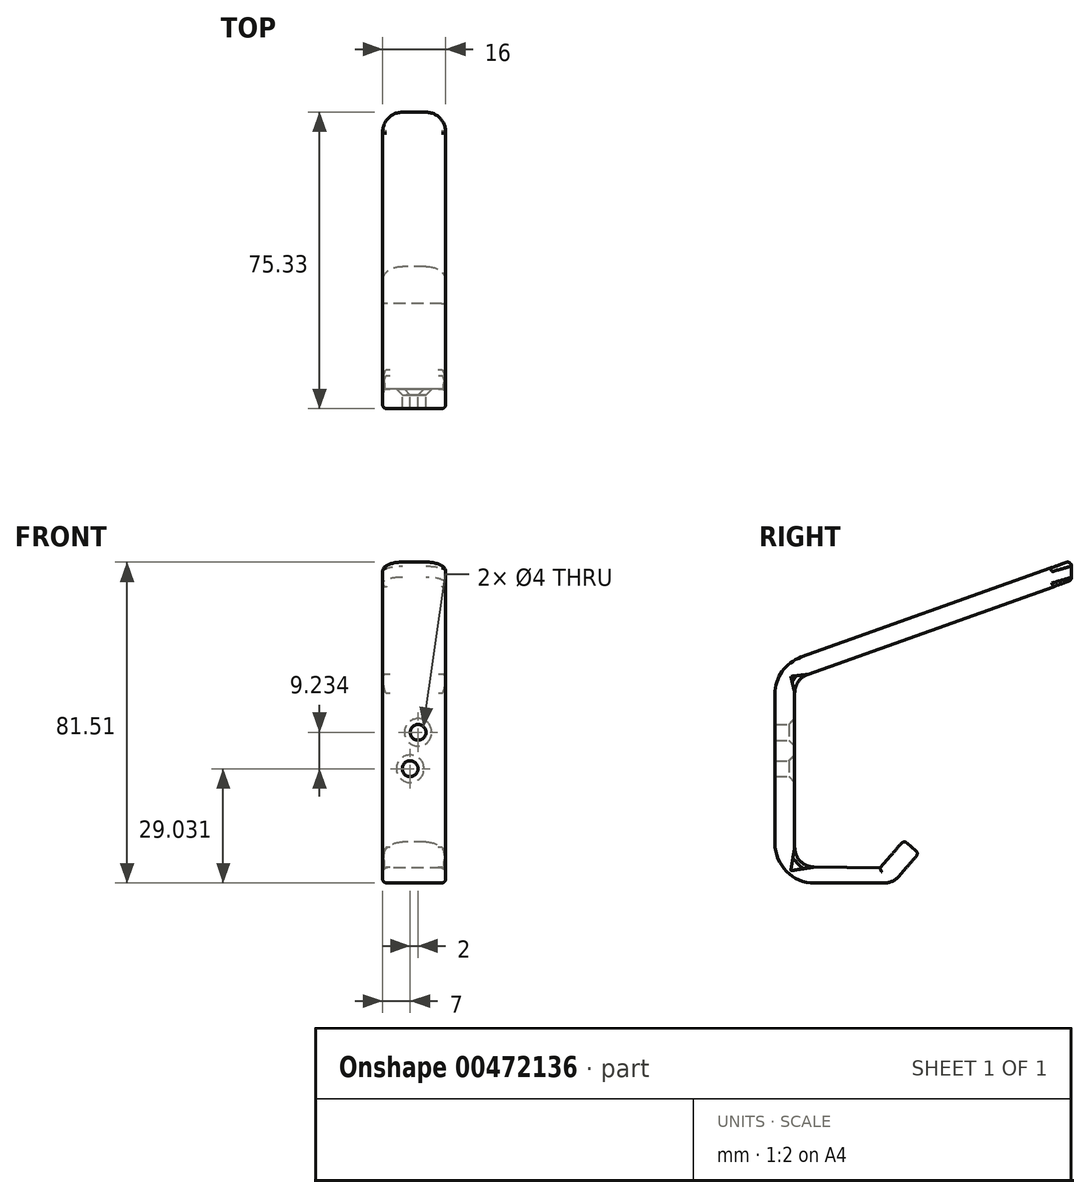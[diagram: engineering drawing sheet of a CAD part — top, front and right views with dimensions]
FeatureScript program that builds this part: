
annotation { "Feature Type Name" : "Feature", "Feature Type Description" : "" }
export const myFeature = defineFeature(function(context is Context, id is Id, definition is map)
    precondition{}
    {
        {
            var Q0;
            Q0=qCreatedBy(makeId("Right.planeOp"),FACE);
            var sketch = newSketch(context, id + "F0", { "sketchPlane" : qUnion([Q0])});
            skLineSegment(sketch, "E0", {"start": v(0, 0) * mm, "end": v(0, 55) * mm});
            skLineSegment(sketch, "E1", {"start": v(0, 0) * mm, "end": v(30, 0) * mm});
            skLineSegment(sketch, "E2", {"start": v(30, 0) * mm, "end": v(36.55, 7.55) * mm});
            skLineSegment(sketch, "E3", {"start": v(0, 55) * mm, "end": v(75.33, 81.93) * mm});
            skLineSegment(sketch, "E4", {"start": v(36.55, 7.55) * mm, "end": v(32.78, 10.83) * mm});
            skLineSegment(sketch, "E5", {"start": v(32.78, 10.83) * mm, "end": v(26.66, 3.78) * mm});
            skPoint(sketch, "E5.endSnap0", {"position": v(33.28, 3.78) * mm});
            skLineSegment(sketch, "E6", {"start": v(75.33, 81.93) * mm, "end": v(75.33, 76.93) * mm});
            skLineSegment(sketch, "E7", {"start": v(75.33, 76.93) * mm, "end": v(5, 51.79) * mm});
            skLineSegment(sketch, "E8", {"start": v(5, 4.33) * mm, "end": v(5, 51.79) * mm});
            skPoint(sketch, "E9.end.orphan", {"position": v(0, -21.36) * mm});
            skPoint(sketch, "E9.start.orphan", {"position": v(5, -21.36) * mm});
            skLineSegment(sketch, "E10", {"start": v(5, 4.33) * mm, "end": v(5, 4.1) * mm});
            skLineSegment(sketch, "E11", {"start": v(26.66, 3.78) * mm, "end": v(5, 4.1) * mm});
            skPoint(sketch, "E12.orphan", {"position": v(-9.92, 4.33) * mm});
            skSolve(sketch);
        }
        {
            var Q0;
            Q0=makeQuery(id+"F0.imprint","IMPRINT",FACE,{"disambiguationData":[TD([[makeQuery(id+"F0.imprint","IMPRINT",EDGE,{"derivedFrom":sQuery(id+"F0.wireOp",EDGE,"E0")}),-1.0]])]});
            extrude(context, id + "F1", {"entities" : qUnion([Q0]), "depth" : 16 * mm, "offsetDistance" : 25 * mm});
        }
        {
            var Q0;
            Q0=makeQuery(id+"F1.opExtrude","SWEPT_EDGE",EDGE,{"disambiguationData":[OSD([sQuery(id+"F0.wireOp",EDGE,"E0"),sQuery(id+"F0.wireOp",EDGE,"E1")])]});
            fillet(context, id + "F2", {"entities" : qUnion([Q0]), "radius" : 10 * mm, "tangentPropagation" : true, "allowEdgeOverflow" : false});
        }
        {
            var Q0;
            Q0=makeQuery(id+"F1.opExtrude","SWEPT_EDGE",EDGE,{"disambiguationData":[OSD([sQuery(id+"F0.wireOp",EDGE,"E0"),sQuery(id+"F0.wireOp",EDGE,"E3")])]});
            fillet(context, id + "F3", {"entities" : qUnion([Q0]), "radius" : 10 * mm, "tangentPropagation" : true, "allowEdgeOverflow" : false});
        }
        {
            var Q0;
            Q0=makeQuery(id+"F1.opExtrude","SWEPT_EDGE",EDGE,{"disambiguationData":[OSD([sQuery(id+"F0.wireOp",EDGE,"E1"),sQuery(id+"F0.wireOp",EDGE,"E2")])]});
            fillet(context, id + "F4", {"entities" : qUnion([Q0]), "radius" : 5 * mm, "tangentPropagation" : true, "allowEdgeOverflow" : false});
        }
        {
            var Q0;
            Q0=makeQuery(id+"F1.opExtrude","CAP_EDGE",EDGE,{"disambiguationData":[OSD([sQuery(id+"F0.wireOp",EDGE,"E11")])],"isStart":true});
            fillet(context, id + "F5", {"entities" : qUnion([Q0]), "radius" : 1 * mm, "tangentPropagation" : true, "allowEdgeOverflow" : false});
        }
        {
            var Q0;
            Q0=makeQuery(id+"F1.opExtrude","CAP_EDGE",EDGE,{"disambiguationData":[OSD([sQuery(id+"F0.wireOp",EDGE,"E5")])],"isStart":true});
            var Q1;
            Q1=makeQuery(id+"F1.opExtrude","CAP_EDGE",EDGE,{"disambiguationData":[OSD([sQuery(id+"F0.wireOp",EDGE,"E5")])],"isStart":false});
            var Q2;
            Q2=makeQuery(id+"F1.opExtrude","SWEPT_EDGE",EDGE,{"disambiguationData":[OSD([sQuery(id+"F0.wireOp",EDGE,"E4"),sQuery(id+"F0.wireOp",EDGE,"E5")])]});
            var Q3;
            Q3=makeQuery(id+"F1.opExtrude","CAP_EDGE",EDGE,{"disambiguationData":[OSD([sQuery(id+"F0.wireOp",EDGE,"E11")])],"isStart":false});
            var Q4;
            Q4=makeQuery(id+"F1.opExtrude","CAP_EDGE",EDGE,{"disambiguationData":[OSD([sQuery(id+"F0.wireOp",EDGE,"E8"),sQuery(id+"F0.wireOp",EDGE,"E10")])],"isStart":true});
            var Q5;
            Q5=makeQuery(id+"F1.opExtrude","CAP_EDGE",EDGE,{"disambiguationData":[OSD([sQuery(id+"F0.wireOp",EDGE,"E8"),sQuery(id+"F0.wireOp",EDGE,"E10")])],"isStart":false});
            var Q6;
            Q6=makeQuery(id+"F1.opExtrude","CAP_EDGE",EDGE,{"disambiguationData":[OSD([sQuery(id+"F0.wireOp",EDGE,"E7")])],"isStart":true});
            var Q7;
            Q7=makeQuery(id+"F1.opExtrude","CAP_EDGE",EDGE,{"disambiguationData":[OSD([sQuery(id+"F0.wireOp",EDGE,"E7")])],"isStart":false});
            var Q8;
            Q8=makeQuery(id+"F1.opExtrude","SWEPT_EDGE",EDGE,{"disambiguationData":[OSD([sQuery(id+"F0.wireOp",EDGE,"E6"),sQuery(id+"F0.wireOp",EDGE,"E7")])]});
            fillet(context, id + "F6", {"entities" : qUnion([Q0, Q1, Q2, Q3, Q4, Q5, Q6, Q7, Q8]), "radius" : 1 * mm, "tangentPropagation" : true, "allowEdgeOverflow" : false});
        }
        {
            var Q0;
            Q0=makeQuery(id+"F1.opExtrude","CAP_EDGE",EDGE,{"disambiguationData":[OSD([sQuery(id+"F0.wireOp",EDGE,"E1")])],"isStart":false});
            var Q1;
            {var subQ0=sQuery(id+"F0.wireOp",EDGE,"E2");var subQ1=sQuery(id+"F0.wireOp",EDGE,"E1");Q1=makeQuery(id+"F4.opFillet","BLEND_EDGE",EDGE,{"blendedFrom":[makeQuery(id+"F1.opExtrude","SWEPT_EDGE",EDGE,{"disambiguationData":[OSD([subQ1,subQ0])]}),makeQuery(id+"F1.opExtrude","CAP_FACE",FACE,{"disambiguationData":[OSD([sQuery(id+"F0.wireOp",EDGE,"E0"),subQ1,subQ0,sQuery(id+"F0.wireOp",EDGE,"E3"),sQuery(id+"F0.wireOp",EDGE,"E4"),sQuery(id+"F0.wireOp",EDGE,"E5"),sQuery(id+"F0.wireOp",EDGE,"E6"),sQuery(id+"F0.wireOp",EDGE,"E7"),sQuery(id+"F0.wireOp",EDGE,"E8"),sQuery(id+"F0.wireOp",EDGE,"E10"),sQuery(id+"F0.wireOp",EDGE,"E11")])],"isStart":false})],"blendedInto":[makeQuery(id+"F1.opExtrude","CAP_FACE",FACE,{"disambiguationData":[OSD([sQuery(id+"F0.wireOp",EDGE,"E0"),subQ1,subQ0,sQuery(id+"F0.wireOp",EDGE,"E3"),sQuery(id+"F0.wireOp",EDGE,"E4"),sQuery(id+"F0.wireOp",EDGE,"E5"),sQuery(id+"F0.wireOp",EDGE,"E6"),sQuery(id+"F0.wireOp",EDGE,"E7"),sQuery(id+"F0.wireOp",EDGE,"E8"),sQuery(id+"F0.wireOp",EDGE,"E10"),sQuery(id+"F0.wireOp",EDGE,"E11")])],"isStart":false})]});}
            var Q2;
            Q2=makeQuery(id+"F1.opExtrude","CAP_EDGE",EDGE,{"disambiguationData":[OSD([sQuery(id+"F0.wireOp",EDGE,"E2")])],"isStart":false});
            var Q3;
            Q3=makeQuery(id+"F1.opExtrude","SWEPT_EDGE",EDGE,{"disambiguationData":[OSD([sQuery(id+"F0.wireOp",EDGE,"E2"),sQuery(id+"F0.wireOp",EDGE,"E4")])]});
            var Q4;
            Q4=makeQuery(id+"F1.opExtrude","CAP_EDGE",EDGE,{"disambiguationData":[OSD([sQuery(id+"F0.wireOp",EDGE,"E2")])],"isStart":true});
            var Q5;
            Q5=makeQuery(id+"F1.opExtrude","CAP_EDGE",EDGE,{"disambiguationData":[OSD([sQuery(id+"F0.wireOp",EDGE,"E1")])],"isStart":true});
            var Q6;
            {var subQ0=sQuery(id+"F0.wireOp",EDGE,"E2");var subQ1=sQuery(id+"F0.wireOp",EDGE,"E1");Q6=makeQuery(id+"F4.opFillet","BLEND_EDGE",EDGE,{"blendedFrom":[makeQuery(id+"F1.opExtrude","SWEPT_EDGE",EDGE,{"disambiguationData":[OSD([subQ1,subQ0])]}),makeQuery(id+"F1.opExtrude","CAP_FACE",FACE,{"disambiguationData":[OSD([sQuery(id+"F0.wireOp",EDGE,"E0"),subQ1,subQ0,sQuery(id+"F0.wireOp",EDGE,"E3"),sQuery(id+"F0.wireOp",EDGE,"E4"),sQuery(id+"F0.wireOp",EDGE,"E5"),sQuery(id+"F0.wireOp",EDGE,"E6"),sQuery(id+"F0.wireOp",EDGE,"E7"),sQuery(id+"F0.wireOp",EDGE,"E8"),sQuery(id+"F0.wireOp",EDGE,"E10"),sQuery(id+"F0.wireOp",EDGE,"E11")])],"isStart":true})],"blendedInto":[makeQuery(id+"F1.opExtrude","CAP_FACE",FACE,{"disambiguationData":[OSD([sQuery(id+"F0.wireOp",EDGE,"E0"),subQ1,subQ0,sQuery(id+"F0.wireOp",EDGE,"E3"),sQuery(id+"F0.wireOp",EDGE,"E4"),sQuery(id+"F0.wireOp",EDGE,"E5"),sQuery(id+"F0.wireOp",EDGE,"E6"),sQuery(id+"F0.wireOp",EDGE,"E7"),sQuery(id+"F0.wireOp",EDGE,"E8"),sQuery(id+"F0.wireOp",EDGE,"E10"),sQuery(id+"F0.wireOp",EDGE,"E11")])],"isStart":true})]});}
            var Q7;
            {var subQ0=sQuery(id+"F0.wireOp",EDGE,"E1");var subQ1=sQuery(id+"F0.wireOp",EDGE,"E0");Q7=makeQuery(id+"F2.opFillet","BLEND_EDGE",EDGE,{"blendedFrom":[makeQuery(id+"F1.opExtrude","SWEPT_EDGE",EDGE,{"disambiguationData":[OSD([subQ1,subQ0])]}),makeQuery(id+"F1.opExtrude","CAP_FACE",FACE,{"disambiguationData":[OSD([subQ1,subQ0,sQuery(id+"F0.wireOp",EDGE,"E2"),sQuery(id+"F0.wireOp",EDGE,"E3"),sQuery(id+"F0.wireOp",EDGE,"E4"),sQuery(id+"F0.wireOp",EDGE,"E5"),sQuery(id+"F0.wireOp",EDGE,"E6"),sQuery(id+"F0.wireOp",EDGE,"E7"),sQuery(id+"F0.wireOp",EDGE,"E8"),sQuery(id+"F0.wireOp",EDGE,"E10"),sQuery(id+"F0.wireOp",EDGE,"E11")])],"isStart":false})],"blendedInto":[makeQuery(id+"F1.opExtrude","CAP_FACE",FACE,{"disambiguationData":[OSD([subQ1,subQ0,sQuery(id+"F0.wireOp",EDGE,"E2"),sQuery(id+"F0.wireOp",EDGE,"E3"),sQuery(id+"F0.wireOp",EDGE,"E4"),sQuery(id+"F0.wireOp",EDGE,"E5"),sQuery(id+"F0.wireOp",EDGE,"E6"),sQuery(id+"F0.wireOp",EDGE,"E7"),sQuery(id+"F0.wireOp",EDGE,"E8"),sQuery(id+"F0.wireOp",EDGE,"E10"),sQuery(id+"F0.wireOp",EDGE,"E11")])],"isStart":false})]});}
            var Q8;
            {var subQ0=sQuery(id+"F0.wireOp",EDGE,"E1");var subQ1=sQuery(id+"F0.wireOp",EDGE,"E0");Q8=makeQuery(id+"F2.opFillet","BLEND_EDGE",EDGE,{"blendedFrom":[makeQuery(id+"F1.opExtrude","SWEPT_EDGE",EDGE,{"disambiguationData":[OSD([subQ1,subQ0])]}),makeQuery(id+"F1.opExtrude","CAP_FACE",FACE,{"disambiguationData":[OSD([subQ1,subQ0,sQuery(id+"F0.wireOp",EDGE,"E2"),sQuery(id+"F0.wireOp",EDGE,"E3"),sQuery(id+"F0.wireOp",EDGE,"E4"),sQuery(id+"F0.wireOp",EDGE,"E5"),sQuery(id+"F0.wireOp",EDGE,"E6"),sQuery(id+"F0.wireOp",EDGE,"E7"),sQuery(id+"F0.wireOp",EDGE,"E8"),sQuery(id+"F0.wireOp",EDGE,"E10"),sQuery(id+"F0.wireOp",EDGE,"E11")])],"isStart":true})],"blendedInto":[makeQuery(id+"F1.opExtrude","CAP_FACE",FACE,{"disambiguationData":[OSD([subQ1,subQ0,sQuery(id+"F0.wireOp",EDGE,"E2"),sQuery(id+"F0.wireOp",EDGE,"E3"),sQuery(id+"F0.wireOp",EDGE,"E4"),sQuery(id+"F0.wireOp",EDGE,"E5"),sQuery(id+"F0.wireOp",EDGE,"E6"),sQuery(id+"F0.wireOp",EDGE,"E7"),sQuery(id+"F0.wireOp",EDGE,"E8"),sQuery(id+"F0.wireOp",EDGE,"E10"),sQuery(id+"F0.wireOp",EDGE,"E11")])],"isStart":true})]});}
            var Q9;
            Q9=makeQuery(id+"F1.opExtrude","CAP_EDGE",EDGE,{"disambiguationData":[OSD([sQuery(id+"F0.wireOp",EDGE,"E0")])],"isStart":true});
            var Q10;
            Q10=makeQuery(id+"F1.opExtrude","CAP_EDGE",EDGE,{"disambiguationData":[OSD([sQuery(id+"F0.wireOp",EDGE,"E0")])],"isStart":false});
            var Q11;
            {var subQ0=sQuery(id+"F0.wireOp",EDGE,"E3");var subQ1=sQuery(id+"F0.wireOp",EDGE,"E0");Q11=makeQuery(id+"F3.opFillet","BLEND_EDGE",EDGE,{"blendedFrom":[makeQuery(id+"F1.opExtrude","SWEPT_EDGE",EDGE,{"disambiguationData":[OSD([subQ1,subQ0])]}),makeQuery(id+"F1.opExtrude","CAP_FACE",FACE,{"disambiguationData":[OSD([subQ1,sQuery(id+"F0.wireOp",EDGE,"E1"),sQuery(id+"F0.wireOp",EDGE,"E2"),subQ0,sQuery(id+"F0.wireOp",EDGE,"E4"),sQuery(id+"F0.wireOp",EDGE,"E5"),sQuery(id+"F0.wireOp",EDGE,"E6"),sQuery(id+"F0.wireOp",EDGE,"E7"),sQuery(id+"F0.wireOp",EDGE,"E8"),sQuery(id+"F0.wireOp",EDGE,"E10"),sQuery(id+"F0.wireOp",EDGE,"E11")])],"isStart":true})],"blendedInto":[makeQuery(id+"F1.opExtrude","CAP_FACE",FACE,{"disambiguationData":[OSD([subQ1,sQuery(id+"F0.wireOp",EDGE,"E1"),sQuery(id+"F0.wireOp",EDGE,"E2"),subQ0,sQuery(id+"F0.wireOp",EDGE,"E4"),sQuery(id+"F0.wireOp",EDGE,"E5"),sQuery(id+"F0.wireOp",EDGE,"E6"),sQuery(id+"F0.wireOp",EDGE,"E7"),sQuery(id+"F0.wireOp",EDGE,"E8"),sQuery(id+"F0.wireOp",EDGE,"E10"),sQuery(id+"F0.wireOp",EDGE,"E11")])],"isStart":true})]});}
            var Q12;
            {var subQ0=sQuery(id+"F0.wireOp",EDGE,"E3");var subQ1=sQuery(id+"F0.wireOp",EDGE,"E0");Q12=makeQuery(id+"F3.opFillet","BLEND_EDGE",EDGE,{"blendedFrom":[makeQuery(id+"F1.opExtrude","SWEPT_EDGE",EDGE,{"disambiguationData":[OSD([subQ1,subQ0])]}),makeQuery(id+"F1.opExtrude","CAP_FACE",FACE,{"disambiguationData":[OSD([subQ1,sQuery(id+"F0.wireOp",EDGE,"E1"),sQuery(id+"F0.wireOp",EDGE,"E2"),subQ0,sQuery(id+"F0.wireOp",EDGE,"E4"),sQuery(id+"F0.wireOp",EDGE,"E5"),sQuery(id+"F0.wireOp",EDGE,"E6"),sQuery(id+"F0.wireOp",EDGE,"E7"),sQuery(id+"F0.wireOp",EDGE,"E8"),sQuery(id+"F0.wireOp",EDGE,"E10"),sQuery(id+"F0.wireOp",EDGE,"E11")])],"isStart":false})],"blendedInto":[makeQuery(id+"F1.opExtrude","CAP_FACE",FACE,{"disambiguationData":[OSD([subQ1,sQuery(id+"F0.wireOp",EDGE,"E1"),sQuery(id+"F0.wireOp",EDGE,"E2"),subQ0,sQuery(id+"F0.wireOp",EDGE,"E4"),sQuery(id+"F0.wireOp",EDGE,"E5"),sQuery(id+"F0.wireOp",EDGE,"E6"),sQuery(id+"F0.wireOp",EDGE,"E7"),sQuery(id+"F0.wireOp",EDGE,"E8"),sQuery(id+"F0.wireOp",EDGE,"E10"),sQuery(id+"F0.wireOp",EDGE,"E11")])],"isStart":false})]});}
            var Q13;
            Q13=makeQuery(id+"F1.opExtrude","CAP_EDGE",EDGE,{"disambiguationData":[OSD([sQuery(id+"F0.wireOp",EDGE,"E3")])],"isStart":true});
            var Q14;
            Q14=makeQuery(id+"F1.opExtrude","CAP_EDGE",EDGE,{"disambiguationData":[OSD([sQuery(id+"F0.wireOp",EDGE,"E3")])],"isStart":false});
            var Q15;
            Q15=makeQuery(id+"F1.opExtrude","SWEPT_EDGE",EDGE,{"disambiguationData":[OSD([sQuery(id+"F0.wireOp",EDGE,"E3"),sQuery(id+"F0.wireOp",EDGE,"E6")])]});
            fillet(context, id + "F7", {"entities" : qUnion([Q0, Q1, Q2, Q3, Q4, Q5, Q6, Q7, Q8, Q9, Q10, Q11, Q12, Q13, Q14, Q15]), "radius" : 1 * mm, "tangentPropagation" : true, "allowEdgeOverflow" : false});
        }
        {
            var Q0;
            Q0=makeQuery(id+"F1.opExtrude","SWEPT_EDGE",EDGE,{"disambiguationData":[OSD([sQuery(id+"F0.wireOp",EDGE,"E10"),sQuery(id+"F0.wireOp",EDGE,"E11")])]});
            fillet(context, id + "F8", {"entities" : qUnion([Q0]), "radius" : 5 * mm, "tangentPropagation" : true, "allowEdgeOverflow" : false});
        }
        {
            var Q0;
            Q0=makeQuery(id+"F1.opExtrude","SWEPT_EDGE",EDGE,{"disambiguationData":[OSD([sQuery(id+"F0.wireOp",EDGE,"E7"),sQuery(id+"F0.wireOp",EDGE,"E8")])]});
            fillet(context, id + "F9", {"entities" : qUnion([Q0]), "radius" : 5 * mm, "tangentPropagation" : true, "allowEdgeOverflow" : false});
        }
        {
            var Q0;
            Q0=makeQuery(id+"F1.opExtrude","CAP_EDGE",EDGE,{"disambiguationData":[OSD([sQuery(id+"F0.wireOp",EDGE,"E6")])],"isStart":true});
            var Q1;
            Q1=makeQuery(id+"F1.opExtrude","CAP_EDGE",EDGE,{"disambiguationData":[OSD([sQuery(id+"F0.wireOp",EDGE,"E6")])],"isStart":false});
            fillet(context, id + "F10", {"entities" : qUnion([Q0, Q1]), "radius" : 5 * mm, "tangentPropagation" : true, "allowEdgeOverflow" : false});
        }
        {
            var Q0;
            Q0=makeQuery(id+"F1.opExtrude","CAP_EDGE",EDGE,{"disambiguationData":[OSD([sQuery(id+"F0.wireOp",EDGE,"E4")])],"isStart":true});
            var Q1;
            Q1=makeQuery(id+"F1.opExtrude","CAP_EDGE",EDGE,{"disambiguationData":[OSD([sQuery(id+"F0.wireOp",EDGE,"E4")])],"isStart":false});
            fillet(context, id + "F11", {"entities" : qUnion([Q0, Q1]), "radius" : 5 * mm, "tangentPropagation" : true, "allowEdgeOverflow" : false});
        }
        {
            var Q0;
            Q0=makeQuery(id+"F1.opExtrude","SWEPT_FACE",FACE,{"disambiguationData":[OSD([sQuery(id+"F0.wireOp",EDGE,"E8"),sQuery(id+"F0.wireOp",EDGE,"E10")])]});
            var sketch = newSketch(context, id + "F12", { "sketchPlane" : qUnion([Q0])});
            skLineSegment(sketch, "E13", {"start": v(-15, 48.27) * mm, "end": v(-15, 38.27) * mm});
            skLineSegment(sketch, "E14", {"start": v(-15, 38.27) * mm, "end": v(-9, 38.27) * mm});
            skLineSegment(sketch, "E15", {"start": v(-1, 9.03) * mm, "end": v(-1, 29.03) * mm});
            skLineSegment(sketch, "E16", {"start": v(-1, 29.03) * mm, "end": v(-7, 29.03) * mm});
            skPoint(sketch, "E17", {"position": v(-9, 38.27) * mm});
            skPoint(sketch, "E18", {"position": v(-7, 29.03) * mm});
            skSolve(sketch);
        }
        {
            var Q0;
            Q0=sQuery(id+"F12.wireOp",VERTEX,"E17");
            var Q1;
            Q1=sQuery(id+"F12.wireOp",VERTEX,"E18");
            var Q2;
            Q2=makeQuery(id+"F1.opExtrude","SWEPT_BODY",BODY,{"disambiguationData":[OSD([sQuery(id+"F0.wireOp",EDGE,"E0"),sQuery(id+"F0.wireOp",EDGE,"E1"),sQuery(id+"F0.wireOp",EDGE,"E2"),sQuery(id+"F0.wireOp",EDGE,"E3"),sQuery(id+"F0.wireOp",EDGE,"E4"),sQuery(id+"F0.wireOp",EDGE,"E5"),sQuery(id+"F0.wireOp",EDGE,"E6"),sQuery(id+"F0.wireOp",EDGE,"E7"),sQuery(id+"F0.wireOp",EDGE,"E8"),sQuery(id+"F0.wireOp",EDGE,"E10"),sQuery(id+"F0.wireOp",EDGE,"E11")])]});
            hole(context, id + "F13", {"style" : HoleStyle.C_SINK, "endStyle" : HoleEndStyle.THROUGH, "holeDiameter" : 4 * mm, "cSinkDiameter" : 7 * mm, "cSinkAngle" : 90 * degree, "isTappedThrough" : true, "tappedDepth" : 12 * mm, "tapClearance" : 3, "locations" : qUnion([Q0, Q1]), "scope" : qUnion([Q2])});
        }
    });
